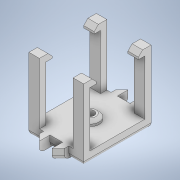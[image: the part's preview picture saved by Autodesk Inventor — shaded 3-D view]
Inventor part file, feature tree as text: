
AUTODESK INVENTOR PART (.ipt)
format: ipt  version: 2020.4 (Build 244396000, 396)  size: 234,496 bytes
history: native  units: in
note: dims shown in document units (in); Inventor stores cm internally (conversion verified against a paired STEP export)
features: extrude x7, sketch x7, chamfer x3, mirror x3, fillet x1
ambient origin geometry x8: Origin, YZ Plane, XZ Plane, XY Plane, X Axis, Y Axis, Z Axis, Center Point
bodies: Solid1 (feature_tree)
feature tree (21):
  extrude  "Extrusion1"  Depth=1.2598in
  extrude  "Extrusion2"  Depth=0.1969in
  extrude  "Extrusion3"  Depth=1.1417in TaperAngle=0.0deg
  chamfer  "Chamfer1"  Distance=0.1181in
  mirror  "Mirror1"
  mirror  "Mirror2"
  extrude  "Extrusion4"  Depth=0.0787in
  extrude  "Extrusion5"  Depth=0.7874in
  chamfer  "Chamfer2"  Distance=0.7874in
  extrude  "Extrusion15"  Depth=0.6299in
  extrude  "Extrusion16"  Depth=0.2362in
  chamfer  "Chamfer6"  Distance=0.0984in
  mirror  "Mirror4"
  fillet  "Fillet2"  Radius=0.1181in
  sketch  "Sketch1"  dims[d0=1.0236in d1=1.2598in]
  sketch  "Sketch2"  dims[d2=0.1969in d3=0.0in d4=0.1969in]
  sketch  "Sketch3"  dims[d5=0.1181in d6=1.1417in d7=0.0in]
  sketch  "Sketch4"  dims[d8=0.1181in d9=0.1181in d10=0.0in]
  sketch  "Sketch5"  dims[d11=0.0787in d12=0.0787in d13=45.0deg d14=0.3406in]
  sketch  "Sketch15"  dims[d15=0.0984in d16=0.0in d17=0.1575in d18=0.7874in d19=0.0in]
  sketch  "Sketch16"  dims[d20=0.0591in d21=0.0787in d22=45.0deg d66=0.6299in d67=0.2362in d68=0.0984in d69=0.0in d70=0.1181in d71=0.1181in d72=0.1969in d73=0.0in d74=0.1181in d75=0.0787in d76=45.0deg d77=0.0787in d78=0.2362in d79=0.2756in d24=0.0197in d25=0.0344in d26=0.0197in d27=0.0344in]
